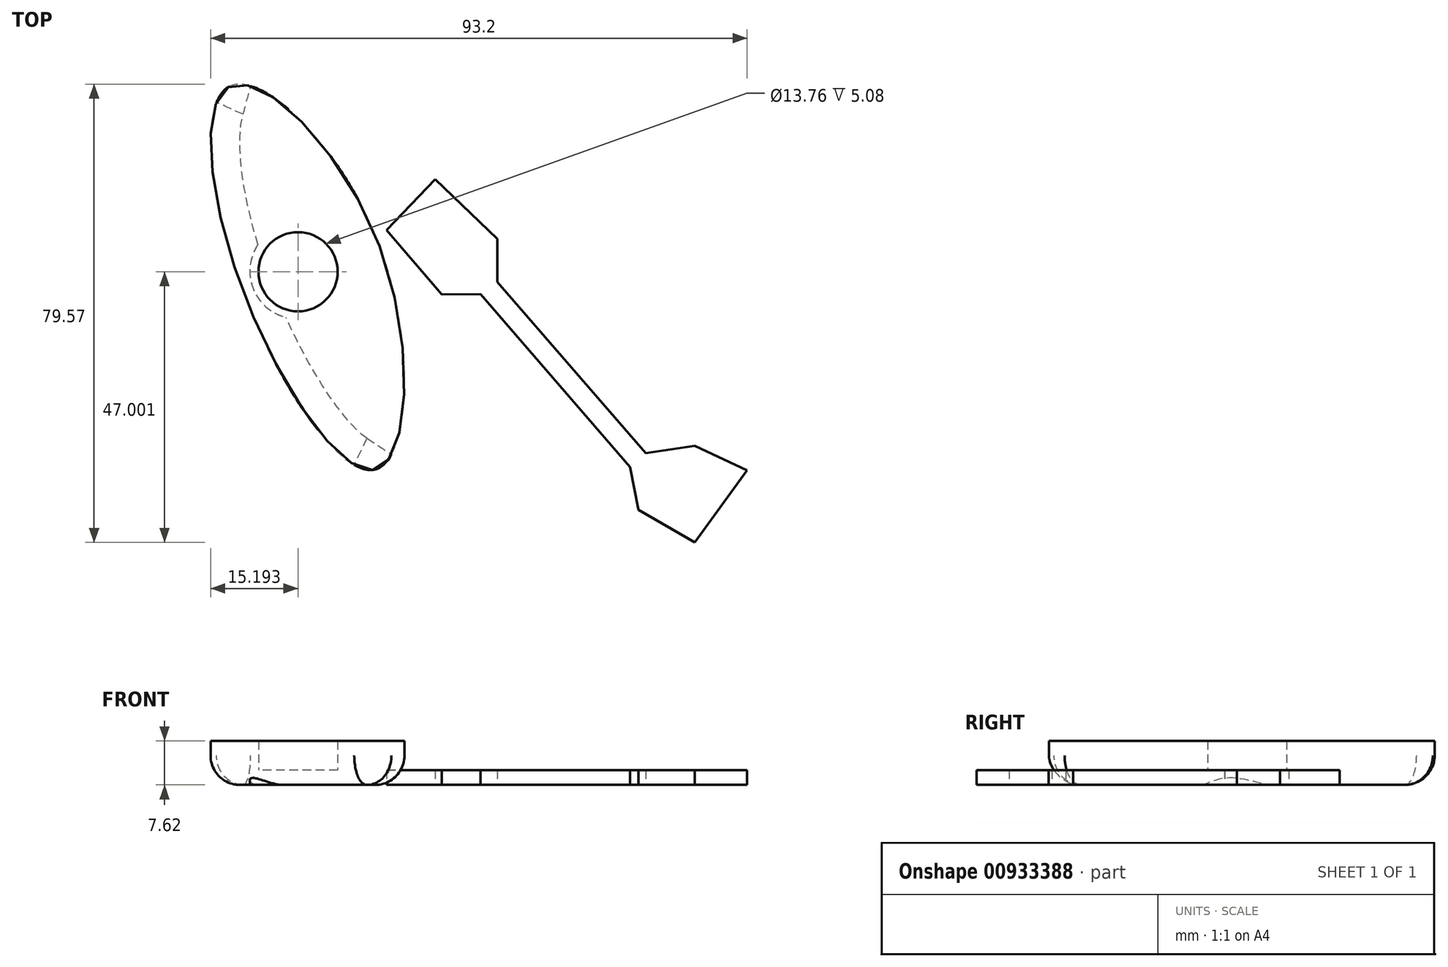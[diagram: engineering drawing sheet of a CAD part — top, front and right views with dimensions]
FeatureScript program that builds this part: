
annotation { "Feature Type Name" : "Feature", "Feature Type Description" : "" }
export const myFeature = defineFeature(function(context is Context, id is Id, definition is map)
    precondition{}
    {
        {
            var Q0;
            Q0=qCreatedBy(makeId("Top.planeOp"),FACE);
            var sketch = newSketch(context, id + "F0", { "sketchPlane" : qUnion([Q0])});
            skFitSpline(sketch, "E0", {"points": [v(-49.84, 43.35) * mm, v(-50.56, 4.6) * mm, v(-74.75, 38.89) * mm, v(-75.47, 71.3) * mm, v(-49.84, 43.35) * mm]});
            skCircle(sketch, "E1", {"center": v(-64, 38.93) * mm, "radius": 6.88 * mm});
            skLineSegment(sketch, "E2", {"start": v(-28.05, 45.91) * mm, "end": v(-18.63, 22.77) * mm});
            skLineSegment(sketch, "E3", {"start": v(-18.63, 22.77) * mm, "end": v(-16.19, 23.77) * mm});
            skLineSegment(sketch, "E4", {"start": v(-16.19, 23.77) * mm, "end": v(-25.52, 46.69) * mm});
            skLineSegment(sketch, "E5", {"start": v(-25.52, 46.69) * mm, "end": v(-25.52, 52.34) * mm});
            skLineSegment(sketch, "E6", {"start": v(-25.52, 52.34) * mm, "end": v(-28.36, 59.32) * mm});
            skLineSegment(sketch, "E7", {"start": v(-28.36, 59.32) * mm, "end": v(-37.06, 55.78) * mm});
            skLineSegment(sketch, "E8", {"start": v(-37.06, 55.78) * mm, "end": v(-34.38, 49.2) * mm});
            skLineSegment(sketch, "E9", {"start": v(-34.38, 49.2) * mm, "end": v(-28.05, 45.91) * mm});
            skSolve(sketch);
        }
        {
            var Q0;
            Q0=makeQuery(id+"F0.imprint","IMPRINT",FACE,{"disambiguationData":[TD([[makeQuery(id+"F0.imprint","IMPRINT",EDGE,{"derivedFrom":sQuery(id+"F0.wireOp",EDGE,"E0")}),-1.0]])]});
            extrude(context, id + "F1", {"entities" : qUnion([Q0]), "depth" : 7.62 * mm, "offsetDistance" : 25.4 * mm});
        }
        {
            var Q0;
            Q0=makeQuery(id+"F1.opExtrude","CAP_EDGE",EDGE,{"disambiguationData":[OSD([sQuery(id+"F0.wireOp",EDGE,"E0")])],"isStart":true});
            fillet(context, id + "F2", {"entities" : qUnion([Q0]), "radius" : 5.08 * mm, "tangentPropagation" : true, "allowEdgeOverflow" : false});
        }
        {
            var Q0;
            Q0=qCreatedBy(makeId("Top.planeOp"),FACE);
            var sketch = newSketch(context, id + "F3", { "sketchPlane" : qUnion([Q0])});
            skCircle(sketch, "E10", {"center": v(-64.1, 39.03) * mm, "radius": 8.28 * mm});
            skLineSegment(sketch, "E11", {"start": v(-32.33, 35.05) * mm, "end": v(-6.35, 5.04) * mm});
            skLineSegment(sketch, "E12", {"start": v(-6.35, 5.04) * mm, "end": v(-3.6, 7.42) * mm});
            skLineSegment(sketch, "E13", {"start": v(-3.6, 7.42) * mm, "end": v(-29.36, 37.17) * mm});
            skLineSegment(sketch, "E14", {"start": v(-29.36, 37.17) * mm, "end": v(-29.36, 44.66) * mm});
            skLineSegment(sketch, "E15", {"start": v(-29.36, 44.66) * mm, "end": v(-40.18, 55) * mm});
            skLineSegment(sketch, "E16", {"start": v(-40.18, 55) * mm, "end": v(-48.63, 46.15) * mm});
            skLineSegment(sketch, "E17", {"start": v(-48.63, 46.15) * mm, "end": v(-39.04, 35.01) * mm});
            skLineSegment(sketch, "E18", {"start": v(-39.04, 35.01) * mm, "end": v(-32.33, 35.05) * mm});
            skLineSegment(sketch, "E19", {"start": v(-3.6, 7.42) * mm, "end": v(4.93, 8.7) * mm});
            skLineSegment(sketch, "E20", {"start": v(4.93, 8.7) * mm, "end": v(14, 4.46) * mm});
            skLineSegment(sketch, "E21", {"start": v(14, 4.46) * mm, "end": v(4.93, -8.07) * mm});
            skLineSegment(sketch, "E22", {"start": v(4.93, -8.07) * mm, "end": v(-4.86, -2.43) * mm});
            skLineSegment(sketch, "E23", {"start": v(-4.86, -2.43) * mm, "end": v(-6.35, 5.04) * mm});
            skSolve(sketch);
        }
        {
            var Q0;
            Q0 = qSketchRegion(id + "F3", true);
            extrude(context, id + "F4", {"entities" : qUnion([Q0]), "operationType" : NewBodyOperationType.ADD, "depth" : 2.54 * mm, "offsetDistance" : 25.4 * mm});
        }
    });
